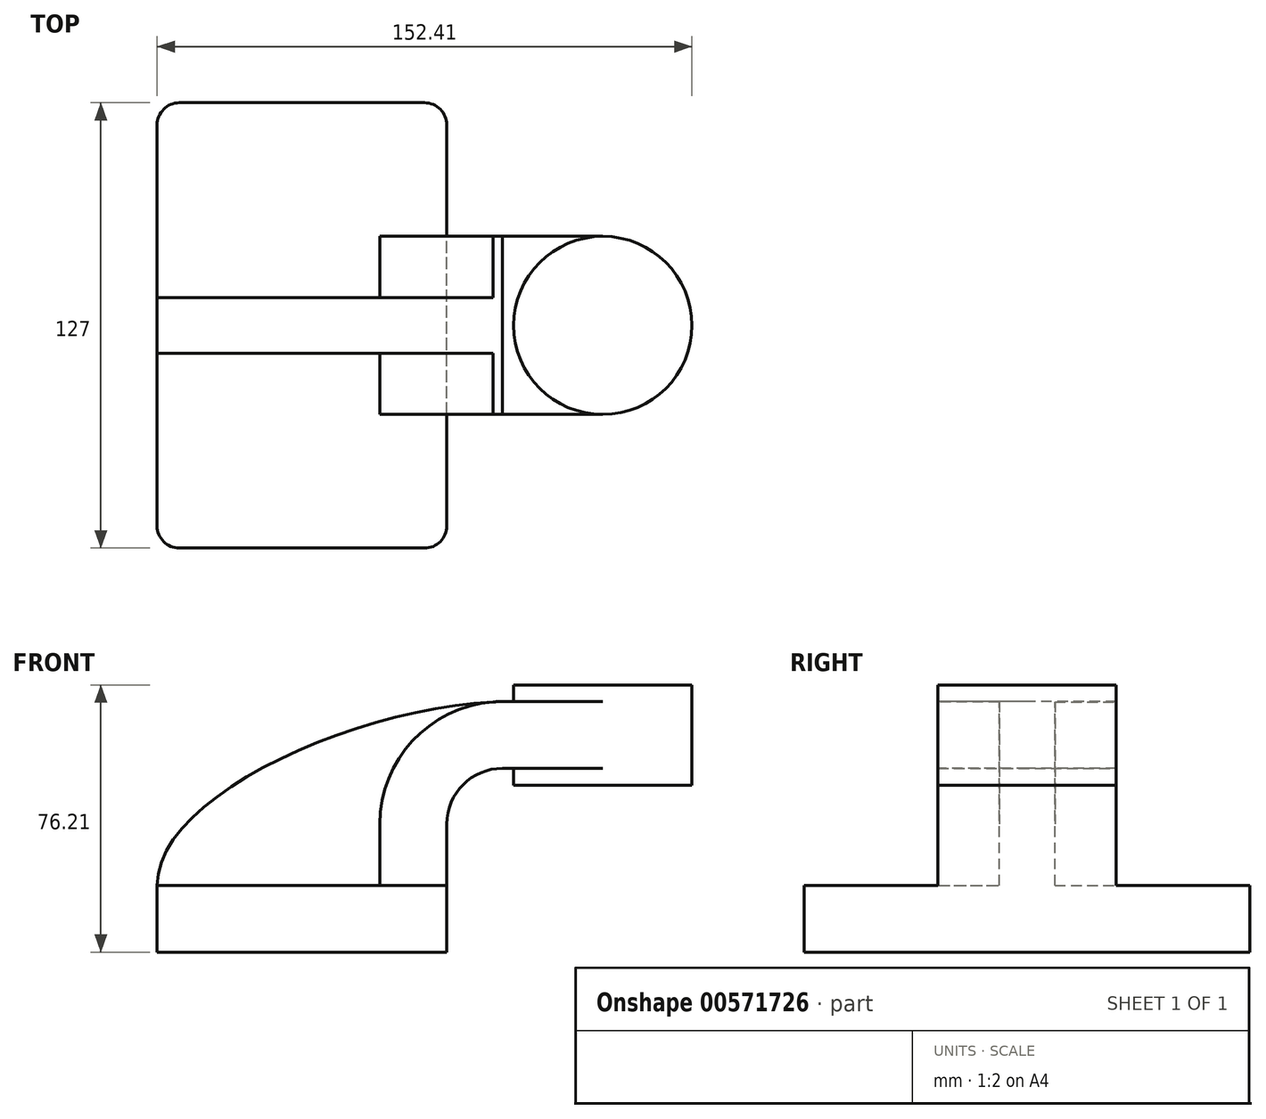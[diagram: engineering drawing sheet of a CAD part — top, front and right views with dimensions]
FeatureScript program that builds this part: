
annotation { "Feature Type Name" : "Feature", "Feature Type Description" : "" }
export const myFeature = defineFeature(function(context is Context, id is Id, definition is map)
    precondition{}
    {
        {
            var Q0;
            Q0=qCreatedBy(makeId("Front.planeOp"),FACE);
            var sketch = newSketch(context, id + "F0", { "sketchPlane" : qUnion([Q0])});
            skLineSegment(sketch, "E0.bottom", {"start": v(-41.28, -9.53) * mm, "end": v(41.28, -9.53) * mm});
            skLineSegment(sketch, "E0.top", {"start": v(-41.28, 9.53) * mm, "end": v(41.28, 9.53) * mm});
            skLineSegment(sketch, "E0.left", {"start": v(-41.28, -9.53) * mm, "end": v(-41.28, 9.53) * mm});
            skLineSegment(sketch, "E0.right", {"start": v(41.28, -9.53) * mm, "end": v(41.28, 9.53) * mm});
            skPoint(sketch, "E0.middle", {"position": v(0, 0) * mm});
            skLineSegment(sketch, "E1.bottom", {"start": v(60.33, 38.1) * mm, "end": v(111.13, 38.1) * mm});
            skLineSegment(sketch, "E1.top", {"start": v(60.32, 66.67) * mm, "end": v(111.13, 66.67) * mm});
            skLineSegment(sketch, "E1.left", {"start": v(60.33, 38.1) * mm, "end": v(60.32, 66.67) * mm});
            skLineSegment(sketch, "E1.right", {"start": v(111.13, 38.1) * mm, "end": v(111.13, 66.67) * mm});
            skPoint(sketch, "E1.middle", {"position": v(85.73, 52.39) * mm});
            skLineSegment(sketch, "E2", {"start": v(41.28, 9.53) * mm, "end": v(41.28, 27) * mm});
            skArc(sketch, "E3", {"start": v(41.27, 27) * mm, "mid": v(45.92, 38.23) * mm, "end": v(57.15, 42.88) * mm});
            skLineSegment(sketch, "E4", {"start": v(57.15, 42.88) * mm, "end": v(85.72, 42.88) * mm});
            skLineSegment(sketch, "E5.0", {"start": v(57.15, 61.93) * mm, "end": v(85.72, 61.93) * mm});
            skArc(sketch, "E5.1", {"start": v(22.22, 27) * mm, "mid": v(32.45, 51.7) * mm, "end": v(57.15, 61.93) * mm});
            skLineSegment(sketch, "E5.2", {"start": v(22.22, 9.53) * mm, "end": v(22.22, 27) * mm});
            skLineSegment(sketch, "E6", {"start": v(85.73, 38.1) * mm, "end": v(85.73, 66.67) * mm});
            skFitSpline(sketch, "E7", {"points": [v(-41.28, 9.53) * mm, v(57.15, 61.93) * mm], "startDerivative": vector(-0.46, 77.32) * mm, "endDerivative": vector(121.8, 3.17) * mm});
            skSolve(sketch);
        }
        {
            var Q0;
            Q0=makeQuery(id+"F0.imprint","IMPRINT",FACE,{"disambiguationData":[TD([[makeQuery(id+"F0.imprint","IMPRINT",EDGE,{"derivedFrom":sQuery(id+"F0.wireOp",EDGE,"E0.bottom")}),1.0]])]});
            extrude(context, id + "F1", {"entities" : qUnion([Q0]), "endBound" : BoundingType.SYMMETRIC, "depth" : 127 * mm, "offsetDistance" : 25.4 * mm});
        }
        {
            var Q0;
            {var subQ1=sQuery(id+"F0.wireOp",EDGE,"E2");Q0=makeQuery(id+"F0.imprint","IMPRINT",FACE,{"disambiguationData":[TD([[makeQuery(id+"F0.imprint","IMPRINT",EDGE,{"derivedFrom":subQ1}),1.0]])]});}
            var Q1;
            {var subQ0=sQuery(id+"F0.wireOp",EDGE,"E4");var subQ1=sQuery(id+"F0.wireOp",EDGE,"E1.left");var subQ2=makeQuery(id+"F0.imprint","INTERSECT",VERTEX,{"derivedFrom":[subQ1,subQ0]});Q1=makeQuery(id+"F0.imprint","IMPRINT",FACE,{"disambiguationData":[TD([[makeQuery(id+"F0.imprint","IMPRINT",EDGE,{"disambiguationData":[TD([[subQ2,-1.0]])],"derivedFrom":subQ1}),-1.0]])]});}
            extrude(context, id + "F2", {"entities" : qUnion([Q0, Q1]), "operationType" : NewBodyOperationType.ADD, "endBound" : BoundingType.SYMMETRIC, "depth" : 50.8 * mm, "offsetDistance" : 25.4 * mm});
        }
        {
            var Q0;
            {var subQ3=sQuery(id+"F0.wireOp",EDGE,"E5.2");Q0=makeQuery(id+"F0.imprint","IMPRINT",FACE,{"disambiguationData":[TD([[makeQuery(id+"F0.imprint","IMPRINT",EDGE,{"derivedFrom":subQ3}),1.0]])]});}
            extrude(context, id + "F3", {"entities" : qUnion([Q0]), "operationType" : NewBodyOperationType.ADD, "endBound" : BoundingType.SYMMETRIC, "depth" : 15.88 * mm, "offsetDistance" : 25.4 * mm});
        }
        {
            var Q0;
            {var subQ4=sQuery(id+"F0.wireOp",EDGE,"E1.right");Q0=makeQuery(id+"F0.imprint","IMPRINT",FACE,{"disambiguationData":[TD([[makeQuery(id+"F0.imprint","IMPRINT",EDGE,{"derivedFrom":subQ4}),1.0]])]});}
            var Q1;
            Q1=sQuery(id+"F0.wireOp",EDGE,"E6");
            revolve(context, id + "F4", {"operationType" : NewBodyOperationType.ADD, "entities" : qUnion([Q0]), "axis" : qUnion([Q1]), "revolveType" : RevolveType.FULL});
        }
        {
            var Q0;
            Q0=makeQuery(id+"F1.opExtrude","CAP_EDGE",EDGE,{"disambiguationData":[OSD([sQuery(id+"F0.wireOp",EDGE,"E0.right")])],"isStart":false});
            var Q1;
            Q1=makeQuery(id+"F1.opExtrude","CAP_EDGE",EDGE,{"disambiguationData":[OSD([sQuery(id+"F0.wireOp",EDGE,"E0.left")])],"isStart":false});
            var Q2;
            Q2=makeQuery(id+"F1.opExtrude","CAP_EDGE",EDGE,{"disambiguationData":[OSD([sQuery(id+"F0.wireOp",EDGE,"E0.right")])],"isStart":true});
            var Q3;
            Q3=makeQuery(id+"F1.opExtrude","CAP_EDGE",EDGE,{"disambiguationData":[OSD([sQuery(id+"F0.wireOp",EDGE,"E0.left")])],"isStart":true});
            fillet(context, id + "F5", {"entities" : qUnion([Q0, Q1, Q2, Q3]), "radius" : 6.35 * mm, "tangentPropagation" : true, "allowEdgeOverflow" : false});
        }
    });
